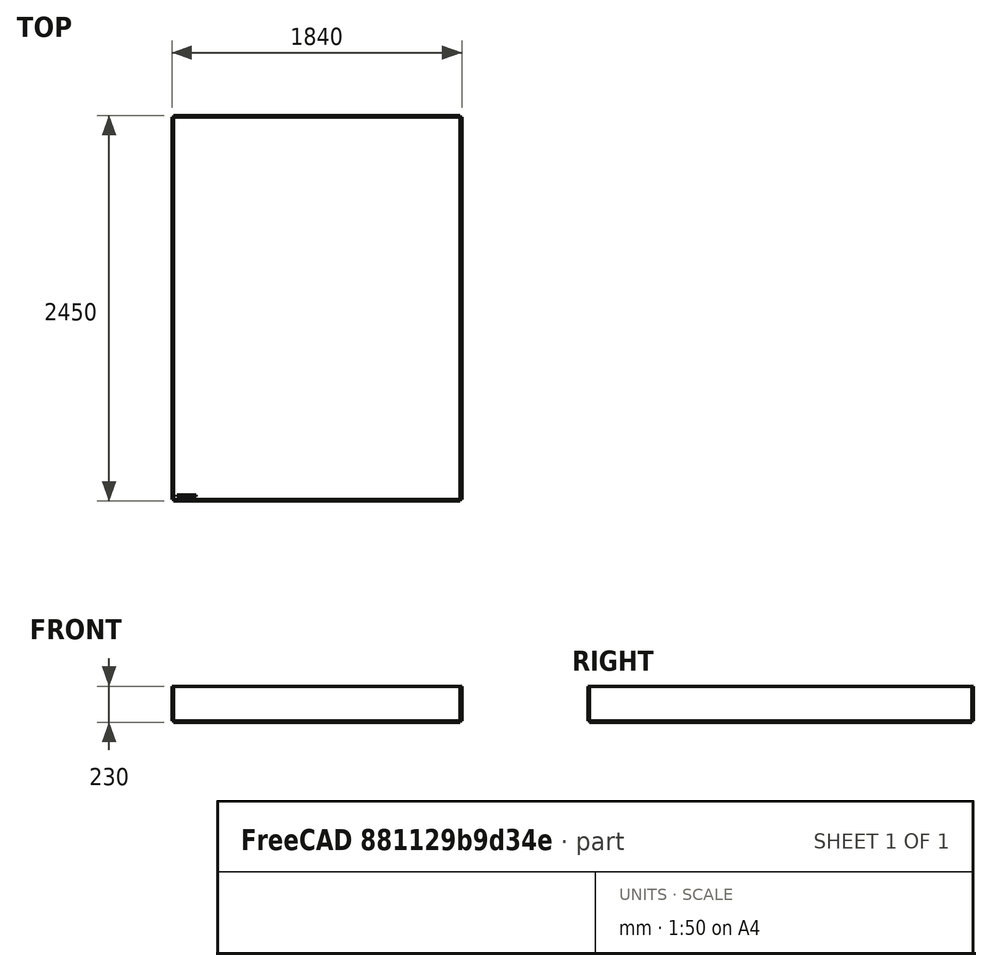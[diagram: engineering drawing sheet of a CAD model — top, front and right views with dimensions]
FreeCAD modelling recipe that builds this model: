
FCSTD DOCUMENT  (FreeCAD 0.21R33771 (Git))
Label: feld
License: All rights reserved
LicenseURL: https://en.wikipedia.org/wiki/All_rights_reserved
objects: Part::Part2DObjectPython×14, Part::Box×5, App::LinkGroup×3, PartDesign::Body×1, Part::Extrusion×1
note: 21 computed .brp shape members not serialized (recipe doc carries the construction recipe); baked Part::Feature solids carry a one-line shape summary decoded from their .brp

FEATURE [PartDesign::Body] Body
  Origin = -> Origin
FEATURE [Part::Part2DObjectPython] Rectangle  # Draft 2D object (typed FeaturePython)
  Area = 4.4226e+06
  ChamferSize = 0
  Columns = 1
  FilletRadius = 0
  Height = 2430
  Length = 1820
  MakeFace = true
  Rows = 1
FEATURE [Part::Extrusion] Extrude  label="field"
  Base = -> Rectangle
  Dir = (0,0,1)
  DirMode = 2
  FaceMakerClass = Part::FaceMakerBullseye
  LengthFwd = 10
  LengthRev = 0
  Solid = false
  Symmetric = false
FEATURE [Part::Box] Box  label="wall"
  AttacherType = Attacher::AttachEngine3D
  Height = 220
  Length = 10
  Placement = pos=(-10,0,10) rot=(0,0,1;0rad)
  Width = 2430
FEATURE [Part::Box] Box001  label="wall2"
  AttacherType = Attacher::AttachEngine3D
  Height = 220
  Length = 10
  Placement = pos=(1820,0,10) rot=(0,0,1;0rad)
  Width = 2430
FEATURE [Part::Box] Box002  label="wall003"
  AttacherType = Attacher::AttachEngine3D
  Height = 220
  Length = 1820
  Placement = pos=(0,-10,10) rot=(0,0,1;0rad)
  Width = 10
FEATURE [Part::Box] Box003  label="wall004"
  AttacherType = Attacher::AttachEngine3D
  Height = 220
  Length = 1820
  Placement = pos=(0,2430,10) rot=(0,0,1;0rad)
  Width = 10
FEATURE [Part::Box] Box004  label="Kubus"
  AttacherType = Attacher::AttachEngine3D
  Height = 5.05
  Length = 120
  Placement = pos=(22,19,5) rot=(0,0,1;0rad)
  Width = 10
FEATURE [Part::Part2DObjectPython] Rectangle001  label="playfield"  # Draft 2D object (typed FeaturePython)
  Area = 3.4602e+06
  ChamferSize = 0
  Columns = 1
  FilletRadius = 0
  Height = 2190
  Length = 1580
  MakeFace = true
  Rows = 1
FEATURE [Part::Part2DObjectPython] Rectangle002  label="line"  # Draft 2D object (typed FeaturePython)
  Area = 43800
  ChamferSize = 0
  Columns = 1
  FilletRadius = 0
  Height = 2190
  Length = -20
  MakeFace = true
  Rows = 1
FEATURE [Part::Part2DObjectPython] Rectangle003  label="line001"  # Draft 2D object (typed FeaturePython)
  Area = 43800
  ChamferSize = 0
  Columns = 1
  FilletRadius = 0
  Height = 2190
  Length = -20
  MakeFace = true
  Placement = pos=(1600,0,0) rot=(0,0,1;0rad)
  Rows = 1
FEATURE [Part::Part2DObjectPython] Rectangle004  label="line002"  # Draft 2D object (typed FeaturePython)
  Area = 32400
  ChamferSize = 0
  Columns = 1
  FilletRadius = 0
  Height = -20
  Length = -1620
  MakeFace = true
  Placement = pos=(1600,0,0) rot=(0,0,1;0rad)
  Rows = 1
FEATURE [Part::Part2DObjectPython] Rectangle005  label="line003"  # Draft 2D object (typed FeaturePython)
  Area = 32400
  ChamferSize = 0
  Columns = 1
  FilletRadius = 0
  Height = -20
  Length = -1620
  MakeFace = true
  Placement = pos=(1600,2210,0) rot=(0,0,1;0rad)
  Rows = 1
FEATURE [Part::Part2DObjectPython] Rectangle006  label="wall005"  # Draft 2D object (typed FeaturePython)
  Area = 72800
  ChamferSize = 0
  Columns = 1
  FilletRadius = 0
  Height = 40
  Length = 1820
  MakeFace = true
  Placement = pos=(0,-190,0) rot=(0,0,1;0rad)
  Rows = 1
FEATURE [Part::Part2DObjectPython] Rectangle007  label="wall006"  # Draft 2D object (typed FeaturePython)
  Area = 97200
  ChamferSize = 0
  Columns = 1
  FilletRadius = 0
  Height = 2430
  Length = 40
  MakeFace = true
  Placement = pos=(-40,-150,0) rot=(0,0,1;0rad)
  Rows = 1
FEATURE [Part::Part2DObjectPython] Rectangle008  label="wall007"  # Draft 2D object (typed FeaturePython)
  Area = 72800
  ChamferSize = 0
  Columns = 1
  FilletRadius = 0
  Height = 40
  Length = 1820
  MakeFace = true
  Placement = pos=(0,2280,0) rot=(0,0,1;0rad)
  Rows = 1
FEATURE [Part::Part2DObjectPython] Rectangle009  label="wall008"  # Draft 2D object (typed FeaturePython)
  Area = 97200
  ChamferSize = 0
  Columns = 1
  FilletRadius = 0
  Height = 2430
  Length = 40
  MakeFace = true
  Placement = pos=(1820,-150,0) rot=(0,0,1;0rad)
  Rows = 1
FEATURE [App::LinkGroup] LinkGroup  label="walls"
  ElementList = -> [Rectangle009,Rectangle008,Rectangle007,Rectangle006]
  LinkMode = 0
  Placement = pos=(-120,29.9999,0) rot=(0,0,1;0rad)
FEATURE [App::LinkGroup] LinkGroup001  label="outlines"
  ElementList = -> [Rectangle005,Rectangle004,Rectangle003,Rectangle002]
  LinkMode = 0
FEATURE [Part::Part2DObjectPython] Rectangle010  label="outeraerea"  # Draft 2D object (typed FeaturePython)
  Area = 223000
  ChamferSize = 0
  Columns = 1
  FilletRadius = 0
  Height = 2230
  Length = -100
  MakeFace = true
  Placement = pos=(-20,-20,0) rot=(0,0,1;0rad)
  Rows = 1
FEATURE [Part::Part2DObjectPython] Rectangle011  label="outeraerea001"  # Draft 2D object (typed FeaturePython)
  Area = 223000
  ChamferSize = 0
  Columns = 1
  FilletRadius = 0
  Height = 2230
  Length = 100
  MakeFace = true
  Placement = pos=(1600,-20,0) rot=(0,0,1;0rad)
  Rows = 1
FEATURE [Part::Part2DObjectPython] Rectangle012  label="outeraerea002"  # Draft 2D object (typed FeaturePython)
  Area = 182000
  ChamferSize = 0
  Columns = 1
  FilletRadius = 0
  Height = -100
  Length = 1820
  MakeFace = true
  Placement = pos=(-120,-20,0) rot=(0,0,1;0rad)
  Rows = 1
FEATURE [Part::Part2DObjectPython] Rectangle013  label="outeraerea003"  # Draft 2D object (typed FeaturePython)
  Area = 182000
  ChamferSize = 0
  Columns = 1
  FilletRadius = 0
  Height = 100
  Length = 1820
  MakeFace = true
  Placement = pos=(-120,2210,0) rot=(0,0,1;0rad)
  Rows = 1
FEATURE [App::LinkGroup] LinkGroup002  label="out"
  ElementList = -> [Rectangle013,Rectangle012,Rectangle011,Rectangle010]
  LinkMode = 0
